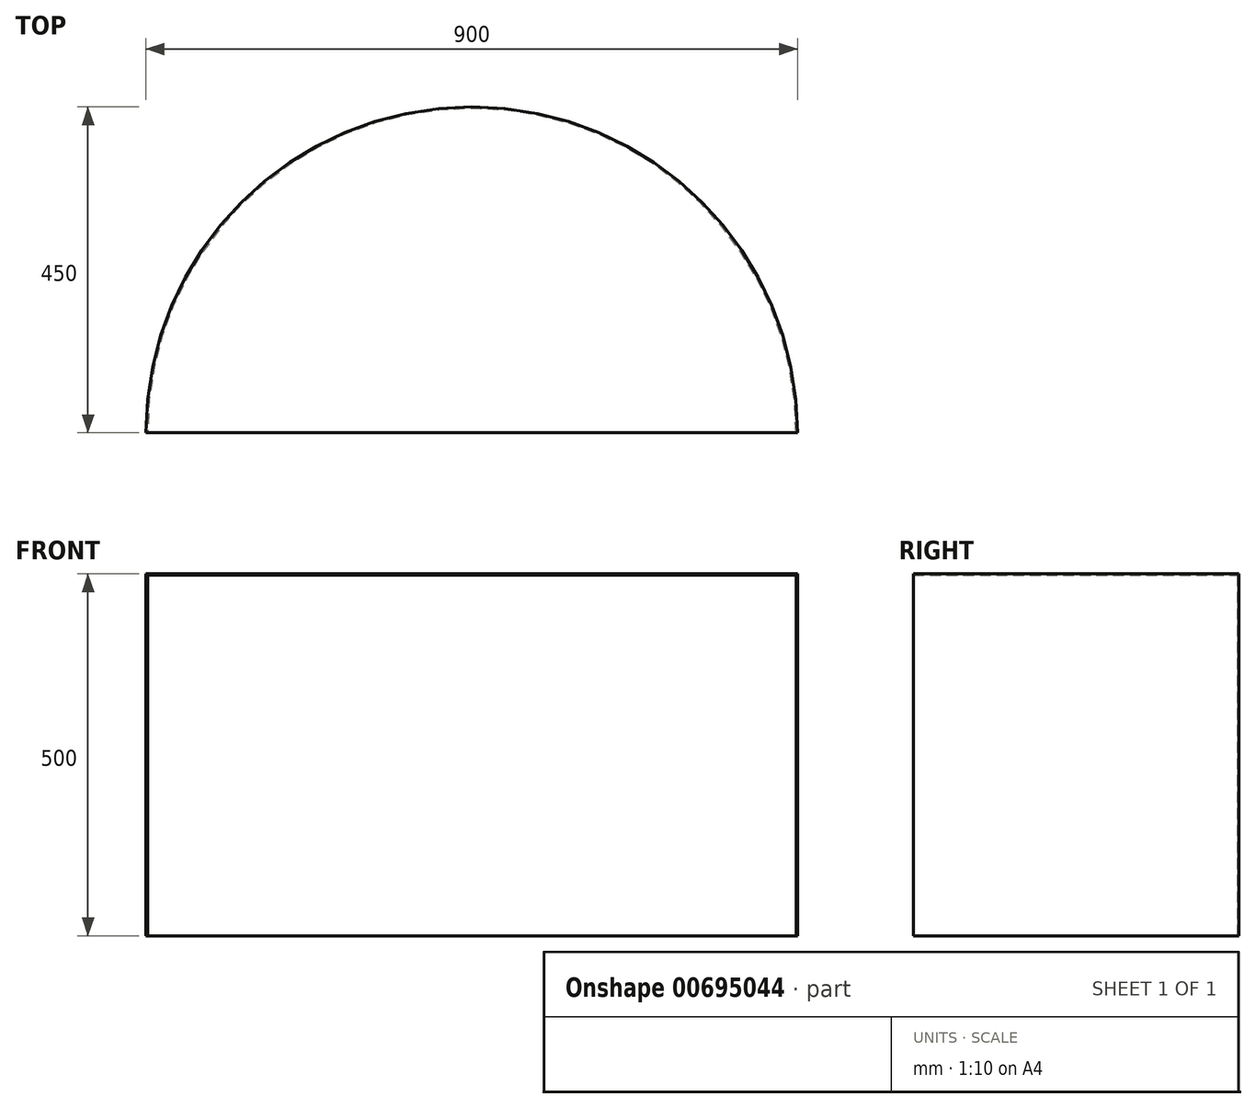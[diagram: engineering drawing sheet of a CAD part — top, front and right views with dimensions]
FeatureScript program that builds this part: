
annotation { "Feature Type Name" : "Feature", "Feature Type Description" : "" }
export const myFeature = defineFeature(function(context is Context, id is Id, definition is map)
    precondition{}
    {
        {
            var Q0;
            Q0=qCreatedBy(makeId("Top.planeOp"),FACE);
            var sketch = newSketch(context, id + "F0", { "sketchPlane" : qUnion([Q0])});
            skLineSegment(sketch, "E0", {"start": v(0, 0) * mm, "end": v(-450, 0) * mm});
            skArc(sketch, "E1", {"start": v(0, 450) * mm, "mid": v(-318.2, 318.2) * mm, "end": v(-450, 0) * mm});
            skLineSegment(sketch, "E2", {"start": v(0, 0) * mm, "end": v(0, 450) * mm});
            skSolve(sketch);
        }
        {
            var Q0;
            Q0=makeQuery(id+"F0.imprint","IMPRINT",FACE,{"disambiguationData":[TD([[makeQuery(id+"F0.imprint","IMPRINT",EDGE,{"derivedFrom":sQuery(id+"F0.wireOp",EDGE,"E0")}),-1.0]])]});
            extrude(context, id + "F1", {"entities" : qUnion([Q0]), "depth" : 500 * mm, "offsetDistance" : 25 * mm});
        }
        {
            var Q0;
            Q0=makeQuery(id+"F1.opExtrude","SWEPT_BODY",BODY,{"disambiguationData":[OSD([sQuery(id+"F0.wireOp",EDGE,"E0"),sQuery(id+"F0.wireOp",EDGE,"E1"),sQuery(id+"F0.wireOp",EDGE,"E2")])]});
            var Q1;
            Q1=qCreatedBy(makeId("Right.planeOp"),FACE);
            mirror(context, id + "F2", {"operationType" : NewBodyOperationType.ADD, "entities" : qUnion([Q0]), "mirrorPlane" : qUnion([Q1])});
        }
        {
            var Q0;
            {var subQ0=makeQuery(id+"F1.opExtrude","SWEPT_FACE",FACE,{"disambiguationData":[OSD([sQuery(id+"F0.wireOp",EDGE,"E0")])]});Q0=makeQuery(id+"F2.boolean.opBoolean","MERGE",FACE,{"derivedFrom":[subQ0,makeQuery(id+"F2.opPattern","COPY",FACE,{"derivedFrom":subQ0,"instanceName":"1"})]});}
            shell(context, id + "F3", {"entities" : qUnion([Q0]), "thickness" : 2 * mm});
        }
        {
            var Q0;
            {var subQ0=sQuery(id+"F0.wireOp",EDGE,"E2");var subQ1=sQuery(id+"F0.wireOp",EDGE,"E1");var subQ2=sQuery(id+"F0.wireOp",EDGE,"E0");var subQ3=makeQuery(id+"F1.opExtrude","CAP_FACE",FACE,{"disambiguationData":[OSD([subQ2,subQ1,subQ0])],"isStart":true});Q0=makeQuery(id+"F3.opShell","OFFSET_FACE",FACE,{"disambiguationData":[OSD([subQ2,subQ1,subQ0]),TDD([makeQuery(id+"F2.boolean.opBoolean","MERGE",FACE,{"derivedFrom":[subQ3,makeQuery(id+"F2.opPattern","COPY",FACE,{"derivedFrom":subQ3,"instanceName":"1"})]})])]});}
            var sketch = newSketch(context, id + "F4", { "sketchPlane" : qUnion([Q0])});
            skLineSegment(sketch, "E3.0.0", {"start": v(-448, 0) * mm, "end": v(448, 0) * mm});
            skArc(sketch, "E3.0.1", {"start": v(448, 0) * mm, "mid": v(0, 448) * mm, "end": v(-448, 0) * mm});
            skSolve(sketch);
        }
        {
            var Q0;
            Q0=makeQuery(id+"F4.imprint","IMPRINT",FACE,{"disambiguationData":[TD([[makeQuery(id+"F4.imprint","IMPRINT",EDGE,{"derivedFrom":sQuery(id+"F4.wireOp",EDGE,"E3.0.0")}),-1.0]])]});
            extrude(context, id + "F5", {"entities" : qUnion([Q0]), "operationType" : NewBodyOperationType.REMOVE, "endBound" : BoundingType.UP_TO_NEXT, "oppositeDirection" : true, "depth" : 25 * mm, "offsetDistance" : 25 * mm});
        }
    });
